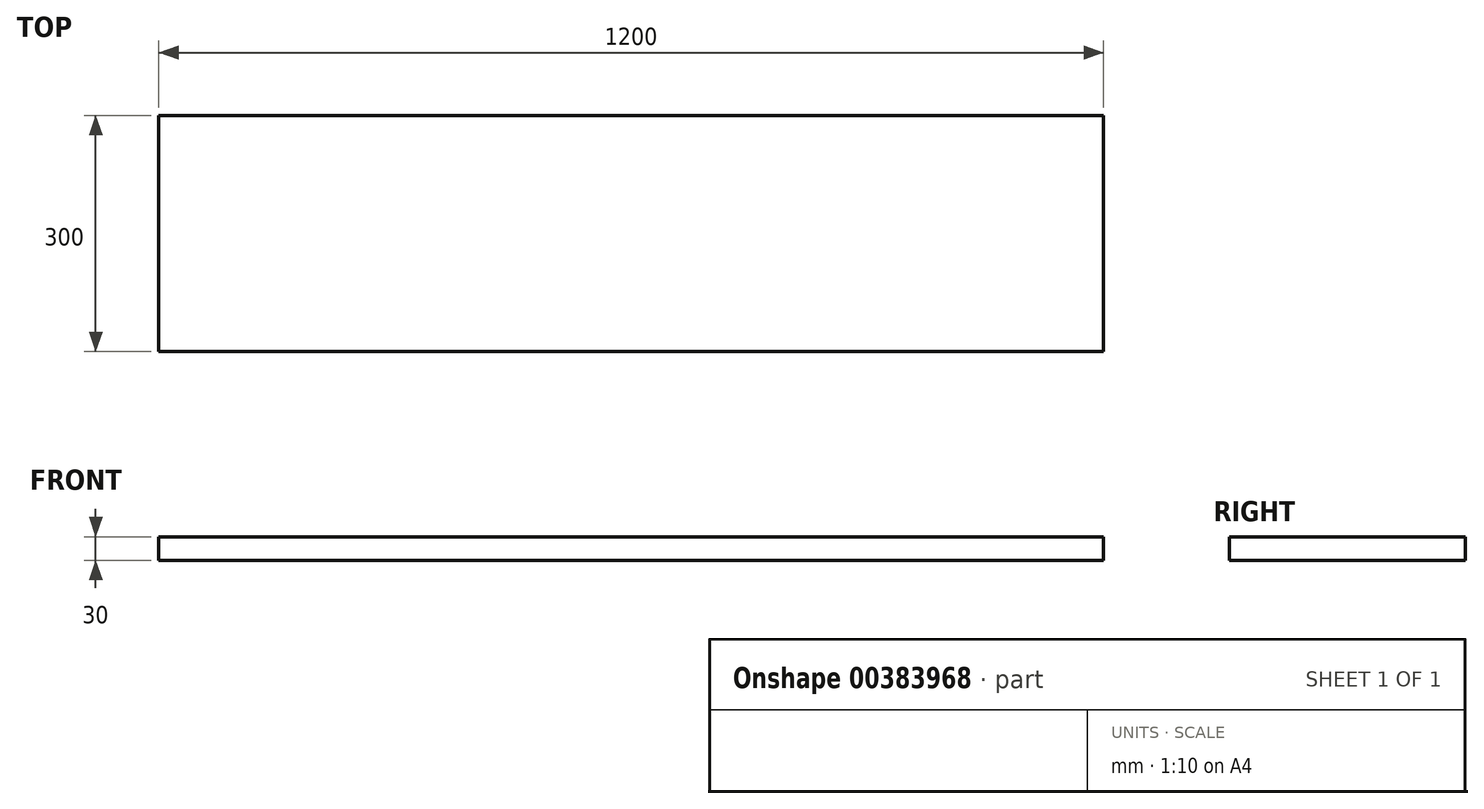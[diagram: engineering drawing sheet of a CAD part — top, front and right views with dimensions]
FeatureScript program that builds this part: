
annotation { "Feature Type Name" : "Feature", "Feature Type Description" : "" }
export const myFeature = defineFeature(function(context is Context, id is Id, definition is map)
    precondition{}
    {
        {
            var Q0;
            Q0=qCreatedBy(makeId("Top.planeOp"),FACE);
            var sketch = newSketch(context, id + "F0", { "sketchPlane" : qUnion([Q0])});
            skLineSegment(sketch, "E0.bottom", {"start": v(-600, 150) * mm, "end": v(600, 150) * mm});
            skLineSegment(sketch, "E0.top", {"start": v(-600, -150) * mm, "end": v(600, -150) * mm});
            skLineSegment(sketch, "E0.left", {"start": v(-600, 150) * mm, "end": v(-600, -150) * mm});
            skLineSegment(sketch, "E0.right", {"start": v(600, 150) * mm, "end": v(600, -150) * mm});
            skPoint(sketch, "E0.middle", {"position": v(0, 0) * mm});
            skSolve(sketch);
        }
        {
            var Q0;
            Q0 = qSketchRegion(id + "F0", true);
            extrude(context, id + "F1", {"entities" : qUnion([Q0]), "endBound" : BoundingType.SYMMETRIC, "depth" : 30 * mm});
        }
    });
